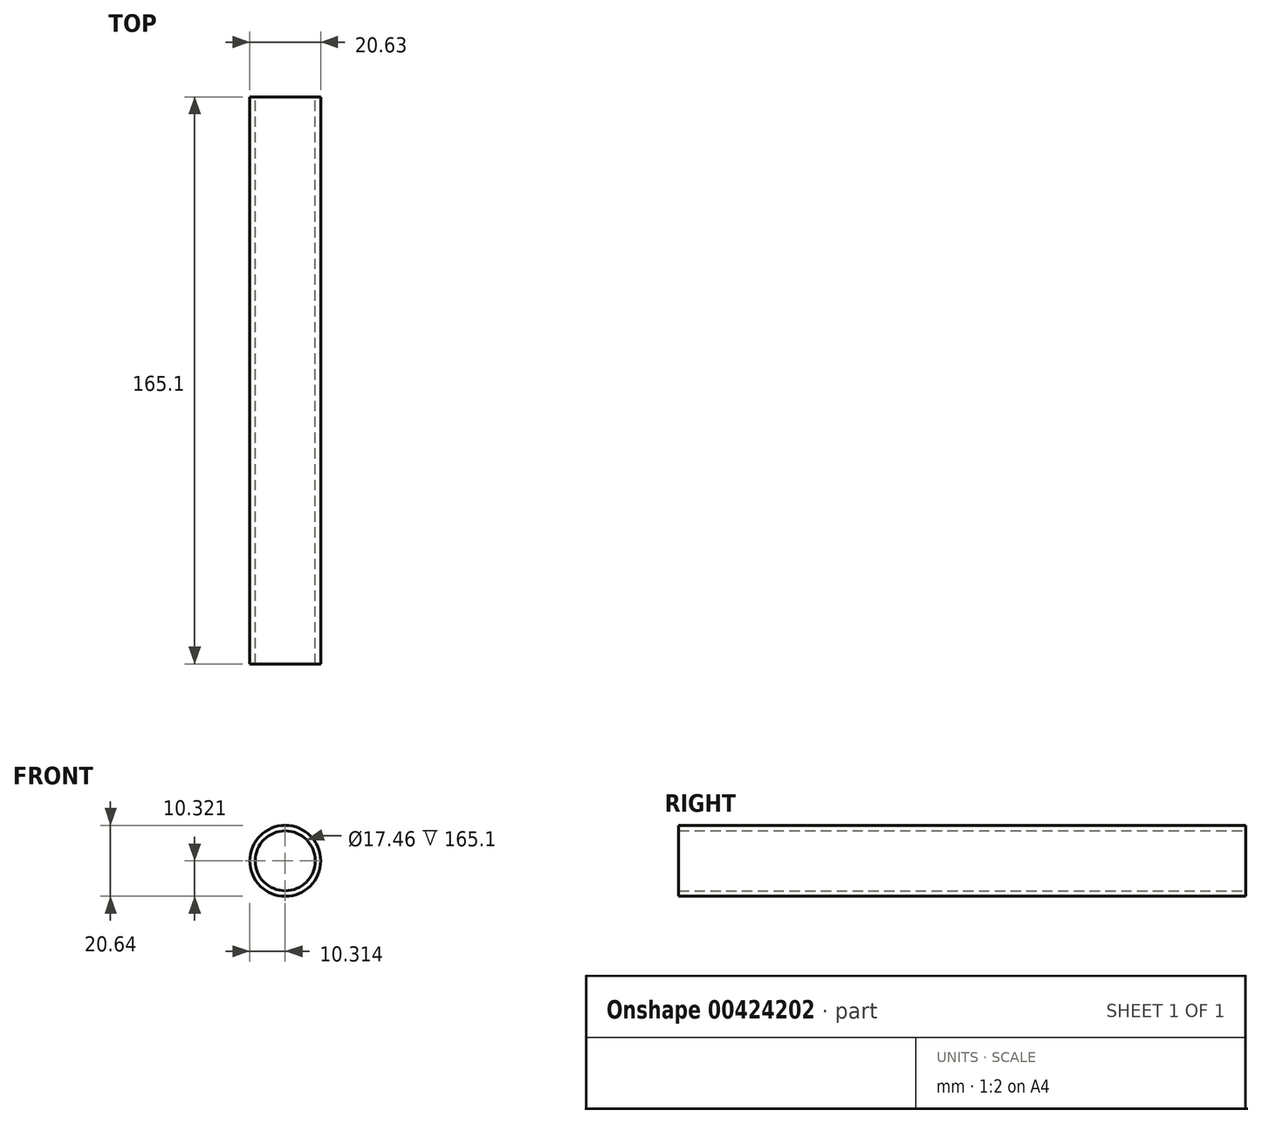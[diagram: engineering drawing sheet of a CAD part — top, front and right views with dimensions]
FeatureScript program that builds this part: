
annotation { "Feature Type Name" : "Feature", "Feature Type Description" : "" }
export const myFeature = defineFeature(function(context is Context, id is Id, definition is map)
    precondition{}
    {
        {
            var Q0;
            Q0=qCreatedBy(makeId("Front.planeOp"),FACE);
            var sketch = newSketch(context, id + "F0", { "sketchPlane" : qUnion([Q0])});
            skCircle(sketch, "E0", {"center": v(-0.78, -0.26) * mm, "radius": 10.32 * mm});
            skCircle(sketch, "E1", {"center": v(-0.78, -0.26) * mm, "radius": 8.73 * mm});
            skSolve(sketch);
        }
        {
            var Q0;
            Q0=qSketchRegion(id+"F0",true);
            extrude(context, id + "F1", {"entities" : qUnion([Q0]), "depth" : 165.1 * mm});
        }
    });
